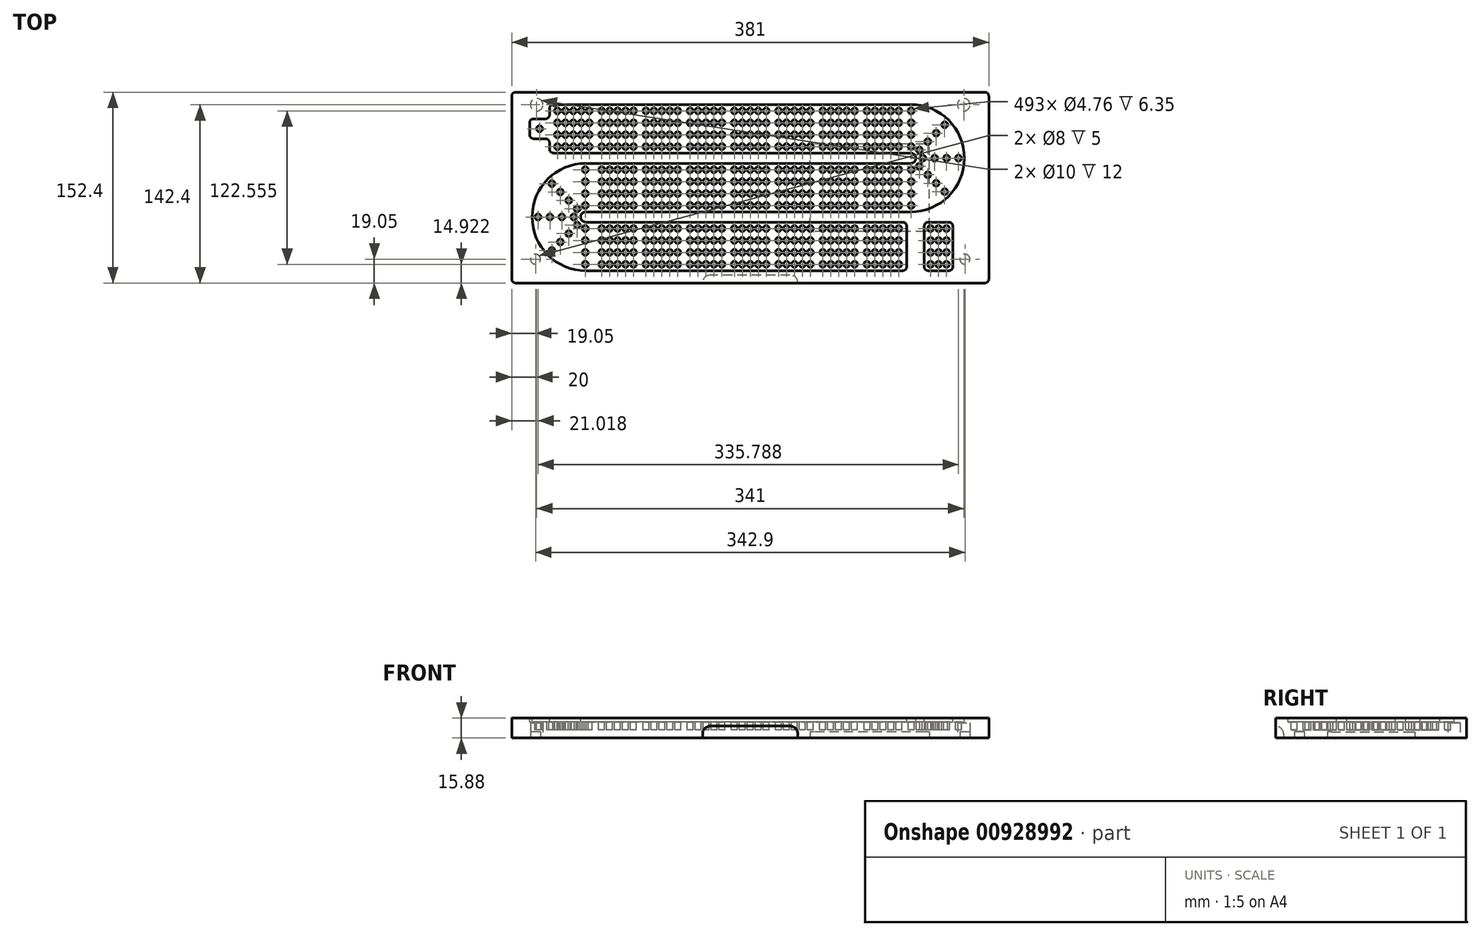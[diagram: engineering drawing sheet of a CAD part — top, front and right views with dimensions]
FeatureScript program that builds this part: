
annotation { "Feature Type Name" : "Feature", "Feature Type Description" : "" }
export const myFeature = defineFeature(function(context is Context, id is Id, definition is map)
    precondition{}
    {
        {
            var Q0;
            Q0=qCreatedBy(makeId("Top.planeOp"),FACE);
            var sketch = newSketch(context, id + "F0", { "sketchPlane" : qUnion([Q0])});
            skLineSegment(sketch, "E0.bottom", {"start": v(190.5, -76.2) * mm, "end": v(-190.5, -76.2) * mm});
            skLineSegment(sketch, "E0.top", {"start": v(190.5, 76.2) * mm, "end": v(-190.5, 76.2) * mm});
            skLineSegment(sketch, "E0.left", {"start": v(190.5, -76.2) * mm, "end": v(190.5, 76.2) * mm});
            skLineSegment(sketch, "E0.right", {"start": v(-190.5, -76.2) * mm, "end": v(-190.5, 76.2) * mm});
            skPoint(sketch, "E0.middle", {"position": v(0, 0) * mm});
            skSolve(sketch);
        }
        {
            var Q0;
            Q0=makeQuery(id+"F0.imprint","IMPRINT",FACE,{"disambiguationData":[TD([[makeQuery(id+"F0.imprint","IMPRINT",EDGE,{"derivedFrom":sQuery(id+"F0.wireOp",EDGE,"E0.bottom")}),-1.0]])]});
            extrude(context, id + "F1", {"entities" : qUnion([Q0]), "oppositeDirection" : true, "depth" : 15.88 * mm, "offsetDistance" : 25.4 * mm});
        }
        {
            var Q0;
            Q0=makeQuery(id+"F1.opExtrude","CAP_FACE",FACE,{"disambiguationData":[OSD([sQuery(id+"F0.wireOp",EDGE,"E0.bottom"),sQuery(id+"F0.wireOp",EDGE,"E0.top"),sQuery(id+"F0.wireOp",EDGE,"E0.left"),sQuery(id+"F0.wireOp",EDGE,"E0.right")])],"isStart":true});
            var sketch = newSketch(context, id + "F2", { "sketchPlane" : qUnion([Q0])});
            skCircle(sketch, "E1", {"center": v(0, -14.29) * mm, "radius": 2.38 * mm});
            skCircle(sketch, "E2.0.1.0", {"center": v(0, -4.76) * mm, "radius": 2.38 * mm});
            skCircle(sketch, "E2.0.2.0", {"center": v(0, 4.76) * mm, "radius": 2.38 * mm});
            skCircle(sketch, "E2.0.3.0", {"center": v(0, 14.29) * mm, "radius": 2.38 * mm});
            skCircle(sketch, "E2.1.0.0", {"center": v(6.35, -14.29) * mm, "radius": 2.38 * mm});
            skCircle(sketch, "E2.1.1.0", {"center": v(6.35, -4.76) * mm, "radius": 2.38 * mm});
            skCircle(sketch, "E2.1.2.0", {"center": v(6.35, 4.76) * mm, "radius": 2.38 * mm});
            skCircle(sketch, "E2.1.3.0", {"center": v(6.35, 14.29) * mm, "radius": 2.38 * mm});
            skCircle(sketch, "E2.2.0.0", {"center": v(12.7, -14.29) * mm, "radius": 2.38 * mm});
            skCircle(sketch, "E2.2.1.0", {"center": v(12.7, -4.76) * mm, "radius": 2.38 * mm});
            skCircle(sketch, "E2.2.2.0", {"center": v(12.7, 4.76) * mm, "radius": 2.38 * mm});
            skCircle(sketch, "E2.2.3.0", {"center": v(12.7, 14.29) * mm, "radius": 2.38 * mm});
            skCircle(sketch, "E3.1.0.0", {"center": v(-6.35, -14.29) * mm, "radius": 2.38 * mm});
            skCircle(sketch, "E3.2.0.0", {"center": v(-12.7, -14.29) * mm, "radius": 2.38 * mm});
            skCircle(sketch, "E4.0.1.0", {"center": v(-6.35, -4.76) * mm, "radius": 2.38 * mm});
            skCircle(sketch, "E4.0.2.0", {"center": v(-6.35, 4.76) * mm, "radius": 2.38 * mm});
            skCircle(sketch, "E4.0.3.0", {"center": v(-6.35, 14.29) * mm, "radius": 2.38 * mm});
            skCircle(sketch, "E5.0.1.0", {"center": v(-12.7, -4.76) * mm, "radius": 2.38 * mm});
            skCircle(sketch, "E5.0.2.0", {"center": v(-12.7, 4.76) * mm, "radius": 2.38 * mm});
            skCircle(sketch, "E5.0.3.0", {"center": v(-12.7, 14.29) * mm, "radius": 2.38 * mm});
            skCircle(sketch, "E6.1.0.0", {"center": v(28.96, 4.76) * mm, "radius": 2.38 * mm});
            skCircle(sketch, "E6.1.0.1", {"center": v(41.66, -14.29) * mm, "radius": 2.38 * mm});
            skCircle(sketch, "E6.1.0.2", {"center": v(41.66, -4.76) * mm, "radius": 2.38 * mm});
            skCircle(sketch, "E6.1.0.3", {"center": v(41.66, 14.29) * mm, "radius": 2.38 * mm});
            skCircle(sketch, "E6.1.0.4", {"center": v(48, 14.29) * mm, "radius": 2.38 * mm});
            skCircle(sketch, "E6.1.0.5", {"center": v(22.6, -14.29) * mm, "radius": 2.38 * mm});
            skCircle(sketch, "E6.1.0.6", {"center": v(28.96, -4.76) * mm, "radius": 2.38 * mm});
            skCircle(sketch, "E6.1.0.7", {"center": v(48, -4.76) * mm, "radius": 2.38 * mm});
            skCircle(sketch, "E6.1.0.8", {"center": v(35.3, 14.29) * mm, "radius": 2.38 * mm});
            skCircle(sketch, "E6.1.0.9", {"center": v(28.96, -14.29) * mm, "radius": 2.38 * mm});
            skCircle(sketch, "E6.1.0.10", {"center": v(22.6, -4.76) * mm, "radius": 2.38 * mm});
            skCircle(sketch, "E6.1.0.11", {"center": v(48, -14.29) * mm, "radius": 2.38 * mm});
            skCircle(sketch, "E6.1.0.12", {"center": v(35.3, -14.29) * mm, "radius": 2.38 * mm});
            skCircle(sketch, "E6.1.0.13", {"center": v(35.3, -4.76) * mm, "radius": 2.38 * mm});
            skCircle(sketch, "E6.1.0.14", {"center": v(28.96, 14.29) * mm, "radius": 2.38 * mm});
            skCircle(sketch, "E6.1.0.15", {"center": v(41.66, 4.76) * mm, "radius": 2.38 * mm});
            skCircle(sketch, "E6.1.0.16", {"center": v(22.6, 14.29) * mm, "radius": 2.38 * mm});
            skCircle(sketch, "E6.1.0.17", {"center": v(48, 4.76) * mm, "radius": 2.38 * mm});
            skCircle(sketch, "E6.1.0.18", {"center": v(22.6, 4.76) * mm, "radius": 2.38 * mm});
            skCircle(sketch, "E6.1.0.19", {"center": v(35.3, 4.76) * mm, "radius": 2.38 * mm});
            skCircle(sketch, "E6.2.0.0", {"center": v(64.26, 4.76) * mm, "radius": 2.38 * mm});
            skCircle(sketch, "E6.2.0.1", {"center": v(76.96, -14.29) * mm, "radius": 2.38 * mm});
            skCircle(sketch, "E6.2.0.2", {"center": v(76.96, -4.76) * mm, "radius": 2.38 * mm});
            skCircle(sketch, "E6.2.0.3", {"center": v(76.96, 14.29) * mm, "radius": 2.38 * mm});
            skCircle(sketch, "E6.2.0.4", {"center": v(83.31, 14.29) * mm, "radius": 2.38 * mm});
            skCircle(sketch, "E6.2.0.5", {"center": v(57.91, -14.29) * mm, "radius": 2.38 * mm});
            skCircle(sketch, "E6.2.0.6", {"center": v(64.26, -4.76) * mm, "radius": 2.38 * mm});
            skCircle(sketch, "E6.2.0.7", {"center": v(83.31, -4.76) * mm, "radius": 2.38 * mm});
            skCircle(sketch, "E6.2.0.8", {"center": v(70.61, 14.29) * mm, "radius": 2.38 * mm});
            skCircle(sketch, "E6.2.0.9", {"center": v(64.26, -14.29) * mm, "radius": 2.38 * mm});
            skCircle(sketch, "E6.2.0.10", {"center": v(57.91, -4.76) * mm, "radius": 2.38 * mm});
            skCircle(sketch, "E6.2.0.11", {"center": v(83.31, -14.29) * mm, "radius": 2.38 * mm});
            skCircle(sketch, "E6.2.0.12", {"center": v(70.61, -14.29) * mm, "radius": 2.38 * mm});
            skCircle(sketch, "E6.2.0.13", {"center": v(70.61, -4.76) * mm, "radius": 2.38 * mm});
            skCircle(sketch, "E6.2.0.14", {"center": v(64.26, 14.29) * mm, "radius": 2.38 * mm});
            skCircle(sketch, "E6.2.0.15", {"center": v(76.96, 4.76) * mm, "radius": 2.38 * mm});
            skCircle(sketch, "E6.2.0.16", {"center": v(57.91, 14.29) * mm, "radius": 2.38 * mm});
            skCircle(sketch, "E6.2.0.17", {"center": v(83.31, 4.76) * mm, "radius": 2.38 * mm});
            skCircle(sketch, "E6.2.0.18", {"center": v(57.91, 4.76) * mm, "radius": 2.38 * mm});
            skCircle(sketch, "E6.2.0.19", {"center": v(70.61, 4.76) * mm, "radius": 2.38 * mm});
            skCircle(sketch, "E6.3.0.0", {"center": v(99.57, 4.76) * mm, "radius": 2.38 * mm});
            skCircle(sketch, "E6.3.0.1", {"center": v(112.27, -14.29) * mm, "radius": 2.38 * mm});
            skCircle(sketch, "E6.3.0.2", {"center": v(112.27, -4.76) * mm, "radius": 2.38 * mm});
            skCircle(sketch, "E6.3.0.3", {"center": v(112.27, 14.29) * mm, "radius": 2.38 * mm});
            skCircle(sketch, "E6.3.0.4", {"center": v(118.62, 14.29) * mm, "radius": 2.38 * mm});
            skCircle(sketch, "E6.3.0.5", {"center": v(93.22, -14.29) * mm, "radius": 2.38 * mm});
            skCircle(sketch, "E6.3.0.6", {"center": v(99.57, -4.76) * mm, "radius": 2.38 * mm});
            skCircle(sketch, "E6.3.0.7", {"center": v(118.62, -4.76) * mm, "radius": 2.38 * mm});
            skCircle(sketch, "E6.3.0.8", {"center": v(105.92, 14.29) * mm, "radius": 2.38 * mm});
            skCircle(sketch, "E6.3.0.9", {"center": v(99.57, -14.29) * mm, "radius": 2.38 * mm});
            skCircle(sketch, "E6.3.0.10", {"center": v(93.22, -4.76) * mm, "radius": 2.38 * mm});
            skCircle(sketch, "E6.3.0.11", {"center": v(118.62, -14.29) * mm, "radius": 2.38 * mm});
            skCircle(sketch, "E6.3.0.12", {"center": v(105.92, -14.29) * mm, "radius": 2.38 * mm});
            skCircle(sketch, "E6.3.0.13", {"center": v(105.92, -4.76) * mm, "radius": 2.38 * mm});
            skCircle(sketch, "E6.3.0.14", {"center": v(99.57, 14.29) * mm, "radius": 2.38 * mm});
            skCircle(sketch, "E6.3.0.15", {"center": v(112.27, 4.76) * mm, "radius": 2.38 * mm});
            skCircle(sketch, "E6.3.0.16", {"center": v(93.22, 14.29) * mm, "radius": 2.38 * mm});
            skCircle(sketch, "E6.3.0.17", {"center": v(118.62, 4.76) * mm, "radius": 2.38 * mm});
            skCircle(sketch, "E6.3.0.18", {"center": v(93.22, 4.76) * mm, "radius": 2.38 * mm});
            skCircle(sketch, "E6.3.0.19", {"center": v(105.92, 4.76) * mm, "radius": 2.38 * mm});
            skLineSegment(sketch, "E6.direction1", {"start": v(-12.7, -14.29) * mm, "end": v(22.6, -14.29) * mm, "construction": true});
            skCircle(sketch, "E7.1.0.0", {"center": v(-48, 4.76) * mm, "radius": 2.38 * mm});
            skCircle(sketch, "E7.1.0.1", {"center": v(-48, -14.29) * mm, "radius": 2.38 * mm});
            skCircle(sketch, "E7.1.0.2", {"center": v(-22.6, 14.29) * mm, "radius": 2.38 * mm});
            skCircle(sketch, "E7.1.0.3", {"center": v(-35.3, 4.76) * mm, "radius": 2.38 * mm});
            skCircle(sketch, "E7.1.0.4", {"center": v(-48, 14.29) * mm, "radius": 2.38 * mm});
            skCircle(sketch, "E7.1.0.5", {"center": v(-35.3, -14.29) * mm, "radius": 2.38 * mm});
            skCircle(sketch, "E7.1.0.6", {"center": v(-35.3, -4.76) * mm, "radius": 2.38 * mm});
            skCircle(sketch, "E7.1.0.7", {"center": v(-48, -4.76) * mm, "radius": 2.38 * mm});
            skCircle(sketch, "E7.1.0.8", {"center": v(-28.96, -4.76) * mm, "radius": 2.38 * mm});
            skCircle(sketch, "E7.1.0.9", {"center": v(-41.66, -4.76) * mm, "radius": 2.38 * mm});
            skCircle(sketch, "E7.1.0.10", {"center": v(-28.96, 4.76) * mm, "radius": 2.38 * mm});
            skCircle(sketch, "E7.1.0.11", {"center": v(-22.6, -4.76) * mm, "radius": 2.38 * mm});
            skCircle(sketch, "E7.1.0.12", {"center": v(-41.66, 14.29) * mm, "radius": 2.38 * mm});
            skCircle(sketch, "E7.1.0.13", {"center": v(-22.6, 4.76) * mm, "radius": 2.38 * mm});
            skCircle(sketch, "E7.1.0.14", {"center": v(-41.66, 4.76) * mm, "radius": 2.38 * mm});
            skCircle(sketch, "E7.1.0.15", {"center": v(-35.3, 14.29) * mm, "radius": 2.38 * mm});
            skCircle(sketch, "E7.1.0.16", {"center": v(-28.96, -14.29) * mm, "radius": 2.38 * mm});
            skCircle(sketch, "E7.1.0.17", {"center": v(-28.96, 14.29) * mm, "radius": 2.38 * mm});
            skCircle(sketch, "E7.1.0.18", {"center": v(-41.66, -14.29) * mm, "radius": 2.38 * mm});
            skCircle(sketch, "E7.1.0.19", {"center": v(-22.6, -14.29) * mm, "radius": 2.38 * mm});
            skCircle(sketch, "E7.2.0.0", {"center": v(-83.31, 4.76) * mm, "radius": 2.38 * mm});
            skCircle(sketch, "E7.2.0.1", {"center": v(-83.31, -14.29) * mm, "radius": 2.38 * mm});
            skCircle(sketch, "E7.2.0.2", {"center": v(-57.91, 14.29) * mm, "radius": 2.38 * mm});
            skCircle(sketch, "E7.2.0.3", {"center": v(-70.61, 4.76) * mm, "radius": 2.38 * mm});
            skCircle(sketch, "E7.2.0.4", {"center": v(-83.31, 14.29) * mm, "radius": 2.38 * mm});
            skCircle(sketch, "E7.2.0.5", {"center": v(-70.61, -14.29) * mm, "radius": 2.38 * mm});
            skCircle(sketch, "E7.2.0.6", {"center": v(-70.61, -4.76) * mm, "radius": 2.38 * mm});
            skCircle(sketch, "E7.2.0.7", {"center": v(-83.31, -4.76) * mm, "radius": 2.38 * mm});
            skCircle(sketch, "E7.2.0.8", {"center": v(-64.26, -4.76) * mm, "radius": 2.38 * mm});
            skCircle(sketch, "E7.2.0.9", {"center": v(-76.96, -4.76) * mm, "radius": 2.38 * mm});
            skCircle(sketch, "E7.2.0.10", {"center": v(-64.26, 4.76) * mm, "radius": 2.38 * mm});
            skCircle(sketch, "E7.2.0.11", {"center": v(-57.91, -4.76) * mm, "radius": 2.38 * mm});
            skCircle(sketch, "E7.2.0.12", {"center": v(-76.96, 14.29) * mm, "radius": 2.38 * mm});
            skCircle(sketch, "E7.2.0.13", {"center": v(-57.91, 4.76) * mm, "radius": 2.38 * mm});
            skCircle(sketch, "E7.2.0.14", {"center": v(-76.96, 4.76) * mm, "radius": 2.38 * mm});
            skCircle(sketch, "E7.2.0.15", {"center": v(-70.61, 14.29) * mm, "radius": 2.38 * mm});
            skCircle(sketch, "E7.2.0.16", {"center": v(-64.26, -14.29) * mm, "radius": 2.38 * mm});
            skCircle(sketch, "E7.2.0.17", {"center": v(-64.26, 14.29) * mm, "radius": 2.38 * mm});
            skCircle(sketch, "E7.2.0.18", {"center": v(-76.96, -14.29) * mm, "radius": 2.38 * mm});
            skCircle(sketch, "E7.2.0.19", {"center": v(-57.91, -14.29) * mm, "radius": 2.38 * mm});
            skCircle(sketch, "E7.3.0.0", {"center": v(-118.62, 4.76) * mm, "radius": 2.38 * mm});
            skCircle(sketch, "E7.3.0.1", {"center": v(-118.62, -14.29) * mm, "radius": 2.38 * mm});
            skCircle(sketch, "E7.3.0.2", {"center": v(-93.22, 14.29) * mm, "radius": 2.38 * mm});
            skCircle(sketch, "E7.3.0.3", {"center": v(-105.92, 4.76) * mm, "radius": 2.38 * mm});
            skCircle(sketch, "E7.3.0.4", {"center": v(-118.62, 14.29) * mm, "radius": 2.38 * mm});
            skCircle(sketch, "E7.3.0.5", {"center": v(-105.92, -14.29) * mm, "radius": 2.38 * mm});
            skCircle(sketch, "E7.3.0.6", {"center": v(-105.92, -4.76) * mm, "radius": 2.38 * mm});
            skCircle(sketch, "E7.3.0.7", {"center": v(-118.62, -4.76) * mm, "radius": 2.38 * mm});
            skCircle(sketch, "E7.3.0.8", {"center": v(-99.57, -4.76) * mm, "radius": 2.38 * mm});
            skCircle(sketch, "E7.3.0.9", {"center": v(-112.27, -4.76) * mm, "radius": 2.38 * mm});
            skCircle(sketch, "E7.3.0.10", {"center": v(-99.57, 4.76) * mm, "radius": 2.38 * mm});
            skCircle(sketch, "E7.3.0.11", {"center": v(-93.22, -4.76) * mm, "radius": 2.38 * mm});
            skCircle(sketch, "E7.3.0.12", {"center": v(-112.27, 14.29) * mm, "radius": 2.38 * mm});
            skCircle(sketch, "E7.3.0.13", {"center": v(-93.22, 4.76) * mm, "radius": 2.38 * mm});
            skCircle(sketch, "E7.3.0.14", {"center": v(-112.27, 4.76) * mm, "radius": 2.38 * mm});
            skCircle(sketch, "E7.3.0.15", {"center": v(-105.92, 14.29) * mm, "radius": 2.38 * mm});
            skCircle(sketch, "E7.3.0.16", {"center": v(-99.57, -14.29) * mm, "radius": 2.38 * mm});
            skCircle(sketch, "E7.3.0.17", {"center": v(-99.57, 14.29) * mm, "radius": 2.38 * mm});
            skCircle(sketch, "E7.3.0.18", {"center": v(-112.27, -14.29) * mm, "radius": 2.38 * mm});
            skCircle(sketch, "E7.3.0.19", {"center": v(-93.22, -14.29) * mm, "radius": 2.38 * mm});
            skCircle(sketch, "E8.0.1.0", {"center": v(93.22, 61.28) * mm, "radius": 2.38 * mm});
            skCircle(sketch, "E8.0.1.1", {"center": v(-83.31, 32.7) * mm, "radius": 2.38 * mm});
            skCircle(sketch, "E8.0.1.2", {"center": v(0, 61.28) * mm, "radius": 2.38 * mm});
            skCircle(sketch, "E8.0.1.3", {"center": v(48, 51.75) * mm, "radius": 2.38 * mm});
            skCircle(sketch, "E8.0.1.4", {"center": v(-41.66, 32.7) * mm, "radius": 2.38 * mm});
            skCircle(sketch, "E8.0.1.5", {"center": v(-105.92, 42.23) * mm, "radius": 2.38 * mm});
            skCircle(sketch, "E8.0.1.6", {"center": v(35.3, 32.7) * mm, "radius": 2.38 * mm});
            skCircle(sketch, "E8.0.1.7", {"center": v(48, 42.23) * mm, "radius": 2.38 * mm});
            skCircle(sketch, "E8.0.1.8", {"center": v(22.6, 42.23) * mm, "radius": 2.38 * mm});
            skCircle(sketch, "E8.0.1.9", {"center": v(-112.27, 61.28) * mm, "radius": 2.38 * mm});
            skCircle(sketch, "E8.0.1.10", {"center": v(0, 42.23) * mm, "radius": 2.38 * mm});
            skCircle(sketch, "E8.0.1.11", {"center": v(76.96, 42.23) * mm, "radius": 2.38 * mm});
            skCircle(sketch, "E8.0.1.12", {"center": v(-70.61, 42.23) * mm, "radius": 2.38 * mm});
            skCircle(sketch, "E8.0.1.13", {"center": v(64.26, 61.28) * mm, "radius": 2.38 * mm});
            skCircle(sketch, "E8.0.1.14", {"center": v(-35.3, 42.23) * mm, "radius": 2.38 * mm});
            skCircle(sketch, "E8.0.1.15", {"center": v(-83.31, 42.23) * mm, "radius": 2.38 * mm});
            skCircle(sketch, "E8.0.1.16", {"center": v(76.96, 32.7) * mm, "radius": 2.38 * mm});
            skCircle(sketch, "E8.0.1.17", {"center": v(-118.62, 32.7) * mm, "radius": 2.38 * mm});
            skCircle(sketch, "E8.0.1.18", {"center": v(35.3, 42.23) * mm, "radius": 2.38 * mm});
            skCircle(sketch, "E8.0.1.19", {"center": v(-99.57, 51.75) * mm, "radius": 2.38 * mm});
            skCircle(sketch, "E8.0.1.20", {"center": v(105.92, 61.28) * mm, "radius": 2.38 * mm});
            skCircle(sketch, "E8.0.1.21", {"center": v(99.57, 61.28) * mm, "radius": 2.38 * mm});
            skCircle(sketch, "E8.0.1.22", {"center": v(70.61, 42.23) * mm, "radius": 2.38 * mm});
            skCircle(sketch, "E8.0.1.23", {"center": v(28.96, 51.75) * mm, "radius": 2.38 * mm});
            skCircle(sketch, "E8.0.1.24", {"center": v(93.22, 51.75) * mm, "radius": 2.38 * mm});
            skCircle(sketch, "E8.0.1.25", {"center": v(48, 32.7) * mm, "radius": 2.38 * mm});
            skCircle(sketch, "E8.0.1.26", {"center": v(-28.96, 61.28) * mm, "radius": 2.38 * mm});
            skCircle(sketch, "E8.0.1.27", {"center": v(-70.61, 61.28) * mm, "radius": 2.38 * mm});
            skCircle(sketch, "E8.0.1.28", {"center": v(-112.27, 42.23) * mm, "radius": 2.38 * mm});
            skCircle(sketch, "E8.0.1.29", {"center": v(-99.57, 32.7) * mm, "radius": 2.38 * mm});
            skCircle(sketch, "E8.0.1.30", {"center": v(6.35, 61.28) * mm, "radius": 2.38 * mm});
            skCircle(sketch, "E8.0.1.31", {"center": v(12.7, 61.28) * mm, "radius": 2.38 * mm});
            skCircle(sketch, "E8.0.1.32", {"center": v(-22.6, 51.75) * mm, "radius": 2.38 * mm});
            skCircle(sketch, "E8.0.1.33", {"center": v(99.57, 42.23) * mm, "radius": 2.38 * mm});
            skCircle(sketch, "E8.0.1.35", {"center": v(64.26, 51.75) * mm, "radius": 2.38 * mm});
            skCircle(sketch, "E8.0.1.36", {"center": v(6.35, 42.23) * mm, "radius": 2.38 * mm});
            skCircle(sketch, "E8.0.1.37", {"center": v(57.91, 61.28) * mm, "radius": 2.38 * mm});
            skCircle(sketch, "E8.0.1.38", {"center": v(-64.26, 32.7) * mm, "radius": 2.38 * mm});
            skCircle(sketch, "E8.0.1.39", {"center": v(-118.62, 42.23) * mm, "radius": 2.38 * mm});
            skCircle(sketch, "E8.0.1.40", {"center": v(-12.7, 61.28) * mm, "radius": 2.38 * mm});
            skCircle(sketch, "E8.0.1.41", {"center": v(-83.31, 51.75) * mm, "radius": 2.38 * mm});
            skCircle(sketch, "E8.0.1.42", {"center": v(112.27, 61.28) * mm, "radius": 2.38 * mm});
            skCircle(sketch, "E8.0.1.43", {"center": v(-70.61, 32.7) * mm, "radius": 2.38 * mm});
            skCircle(sketch, "E8.0.1.44", {"center": v(-28.96, 51.75) * mm, "radius": 2.38 * mm});
            skCircle(sketch, "E8.0.1.45", {"center": v(28.96, 61.28) * mm, "radius": 2.38 * mm});
            skCircle(sketch, "E8.0.1.46", {"center": v(12.7, 42.23) * mm, "radius": 2.38 * mm});
            skCircle(sketch, "E8.0.1.47", {"center": v(-12.7, 51.75) * mm, "radius": 2.38 * mm});
            skCircle(sketch, "E8.0.1.48", {"center": v(-41.66, 42.23) * mm, "radius": 2.38 * mm});
            skCircle(sketch, "E8.0.1.49", {"center": v(64.26, 32.7) * mm, "radius": 2.38 * mm});
            skCircle(sketch, "E8.0.1.50", {"center": v(22.6, 61.28) * mm, "radius": 2.38 * mm});
            skCircle(sketch, "E8.0.1.51", {"center": v(76.96, 61.28) * mm, "radius": 2.38 * mm});
            skCircle(sketch, "E8.0.1.52", {"center": v(-99.57, 42.23) * mm, "radius": 2.38 * mm});
            skCircle(sketch, "E8.0.1.53", {"center": v(93.22, 32.7) * mm, "radius": 2.38 * mm});
            skCircle(sketch, "E8.0.1.54", {"center": v(118.62, 61.28) * mm, "radius": 2.38 * mm});
            skCircle(sketch, "E8.0.1.55", {"center": v(-12.7, 42.23) * mm, "radius": 2.38 * mm});
            skCircle(sketch, "E8.0.1.56", {"center": v(-41.66, 61.28) * mm, "radius": 2.38 * mm});
            skCircle(sketch, "E8.0.1.57", {"center": v(-93.22, 51.75) * mm, "radius": 2.38 * mm});
            skCircle(sketch, "E8.0.1.58", {"center": v(6.35, 51.75) * mm, "radius": 2.38 * mm});
            skCircle(sketch, "E8.0.1.59", {"center": v(118.62, 42.23) * mm, "radius": 2.38 * mm});
            skCircle(sketch, "E8.0.1.60", {"center": v(93.22, 42.23) * mm, "radius": 2.38 * mm});
            skCircle(sketch, "E8.0.1.61", {"center": v(112.27, 42.23) * mm, "radius": 2.38 * mm});
            skCircle(sketch, "E8.0.1.62", {"center": v(-57.91, 51.75) * mm, "radius": 2.38 * mm});
            skCircle(sketch, "E8.0.1.63", {"center": v(-76.96, 61.28) * mm, "radius": 2.38 * mm});
            skCircle(sketch, "E8.0.1.64", {"center": v(-12.7, 32.7) * mm, "radius": 2.38 * mm});
            skCircle(sketch, "E8.0.1.65", {"center": v(83.31, 61.28) * mm, "radius": 2.38 * mm});
            skCircle(sketch, "E8.0.1.66", {"center": v(-93.22, 61.28) * mm, "radius": 2.38 * mm});
            skCircle(sketch, "E8.0.1.67", {"center": v(-57.91, 32.7) * mm, "radius": 2.38 * mm});
            skCircle(sketch, "E8.0.1.68", {"center": v(-99.57, 61.28) * mm, "radius": 2.38 * mm});
            skCircle(sketch, "E8.0.1.69", {"center": v(41.66, 61.28) * mm, "radius": 2.38 * mm});
            skCircle(sketch, "E8.0.1.70", {"center": v(-83.31, 61.28) * mm, "radius": 2.38 * mm});
            skCircle(sketch, "E8.0.1.71", {"center": v(57.91, 42.23) * mm, "radius": 2.38 * mm});
            skCircle(sketch, "E8.0.1.72", {"center": v(-28.96, 42.23) * mm, "radius": 2.38 * mm});
            skCircle(sketch, "E8.0.1.73", {"center": v(105.92, 32.7) * mm, "radius": 2.38 * mm});
            skCircle(sketch, "E8.0.1.74", {"center": v(-6.35, 42.23) * mm, "radius": 2.38 * mm});
            skCircle(sketch, "E8.0.1.75", {"center": v(-35.3, 61.28) * mm, "radius": 2.38 * mm});
            skCircle(sketch, "E8.0.1.76", {"center": v(-105.92, 61.28) * mm, "radius": 2.38 * mm});
            skCircle(sketch, "E8.0.1.77", {"center": v(83.31, 51.75) * mm, "radius": 2.38 * mm});
            skCircle(sketch, "E8.0.1.78", {"center": v(41.66, 42.23) * mm, "radius": 2.38 * mm});
            skCircle(sketch, "E8.0.1.79", {"center": v(-93.22, 42.23) * mm, "radius": 2.38 * mm});
            skCircle(sketch, "E8.0.1.80", {"center": v(28.96, 42.23) * mm, "radius": 2.38 * mm});
            skCircle(sketch, "E8.0.1.81", {"center": v(48, 61.28) * mm, "radius": 2.38 * mm});
            skCircle(sketch, "E8.0.1.82", {"center": v(35.3, 61.28) * mm, "radius": 2.38 * mm});
            skCircle(sketch, "E8.0.1.83", {"center": v(-76.96, 42.23) * mm, "radius": 2.38 * mm});
            skCircle(sketch, "E8.0.1.84", {"center": v(-93.22, 32.7) * mm, "radius": 2.38 * mm});
            skCircle(sketch, "E8.0.1.85", {"center": v(64.26, 42.23) * mm, "radius": 2.38 * mm});
            skCircle(sketch, "E8.0.1.86", {"center": v(-57.91, 42.23) * mm, "radius": 2.38 * mm});
            skCircle(sketch, "E8.0.1.87", {"center": v(-48, 61.28) * mm, "radius": 2.38 * mm});
            skCircle(sketch, "E8.0.1.88", {"center": v(-41.66, 51.75) * mm, "radius": 2.38 * mm});
            skCircle(sketch, "E8.0.1.89", {"center": v(-28.96, 32.7) * mm, "radius": 2.38 * mm});
            skCircle(sketch, "E8.0.1.90", {"center": v(83.31, 42.23) * mm, "radius": 2.38 * mm});
            skCircle(sketch, "E8.0.1.91", {"center": v(-22.6, 42.23) * mm, "radius": 2.38 * mm});
            skCircle(sketch, "E8.0.1.92", {"center": v(-64.26, 61.28) * mm, "radius": 2.38 * mm});
            skCircle(sketch, "E8.0.1.93", {"center": v(-57.91, 61.28) * mm, "radius": 2.38 * mm});
            skCircle(sketch, "E8.0.1.94", {"center": v(70.61, 61.28) * mm, "radius": 2.38 * mm});
            skCircle(sketch, "E8.0.1.95", {"center": v(-118.62, 51.75) * mm, "radius": 2.38 * mm});
            skCircle(sketch, "E8.0.1.96", {"center": v(112.27, 51.75) * mm, "radius": 2.38 * mm});
            skCircle(sketch, "E8.0.1.97", {"center": v(-64.26, 51.75) * mm, "radius": 2.38 * mm});
            skCircle(sketch, "E8.0.1.98", {"center": v(-6.35, 61.28) * mm, "radius": 2.38 * mm});
            skCircle(sketch, "E8.0.1.99", {"center": v(-64.26, 42.23) * mm, "radius": 2.38 * mm});
            skCircle(sketch, "E8.0.1.100", {"center": v(-70.61, 51.75) * mm, "radius": 2.38 * mm});
            skCircle(sketch, "E8.0.1.101", {"center": v(-22.6, 61.28) * mm, "radius": 2.38 * mm});
            skCircle(sketch, "E8.0.1.102", {"center": v(105.92, 42.23) * mm, "radius": 2.38 * mm});
            skCircle(sketch, "E8.0.1.103", {"center": v(-48, 42.23) * mm, "radius": 2.38 * mm});
            skCircle(sketch, "E8.0.1.104", {"center": v(-118.62, 61.28) * mm, "radius": 2.38 * mm});
            skCircle(sketch, "E8.0.1.105", {"center": v(57.91, 32.7) * mm, "radius": 2.38 * mm});
            skCircle(sketch, "E8.0.1.106", {"center": v(0, 32.7) * mm, "radius": 2.38 * mm});
            skCircle(sketch, "E8.0.1.107", {"center": v(0, 51.75) * mm, "radius": 2.38 * mm});
            skCircle(sketch, "E8.0.1.108", {"center": v(-112.27, 51.75) * mm, "radius": 2.38 * mm});
            skCircle(sketch, "E8.0.1.109", {"center": v(-76.96, 51.75) * mm, "radius": 2.38 * mm});
            skCircle(sketch, "E8.0.1.110", {"center": v(-6.35, 51.75) * mm, "radius": 2.38 * mm});
            skCircle(sketch, "E8.0.1.111", {"center": v(118.62, 32.7) * mm, "radius": 2.38 * mm});
            skCircle(sketch, "E8.0.1.112", {"center": v(-112.27, 32.7) * mm, "radius": 2.38 * mm});
            skCircle(sketch, "E8.0.1.113", {"center": v(83.31, 32.7) * mm, "radius": 2.38 * mm});
            skCircle(sketch, "E8.0.1.114", {"center": v(-48, 51.75) * mm, "radius": 2.38 * mm});
            skCircle(sketch, "E8.0.1.115", {"center": v(-6.35, 32.7) * mm, "radius": 2.38 * mm});
            skCircle(sketch, "E8.0.1.116", {"center": v(99.57, 32.7) * mm, "radius": 2.38 * mm});
            skCircle(sketch, "E8.0.1.117", {"center": v(-22.6, 32.7) * mm, "radius": 2.38 * mm});
            skCircle(sketch, "E8.0.1.118", {"center": v(-105.92, 51.75) * mm, "radius": 2.38 * mm});
            skCircle(sketch, "E8.0.1.119", {"center": v(6.35, 32.7) * mm, "radius": 2.38 * mm});
            skCircle(sketch, "E8.0.1.120", {"center": v(28.96, 32.7) * mm, "radius": 2.38 * mm});
            skCircle(sketch, "E8.0.1.121", {"center": v(57.91, 51.75) * mm, "radius": 2.38 * mm});
            skCircle(sketch, "E8.0.1.122", {"center": v(112.27, 32.7) * mm, "radius": 2.38 * mm});
            skCircle(sketch, "E8.0.1.123", {"center": v(118.62, 51.75) * mm, "radius": 2.38 * mm});
            skCircle(sketch, "E8.0.1.124", {"center": v(-105.92, 32.7) * mm, "radius": 2.38 * mm});
            skCircle(sketch, "E8.0.1.125", {"center": v(70.61, 32.7) * mm, "radius": 2.38 * mm});
            skCircle(sketch, "E8.0.1.126", {"center": v(12.7, 32.7) * mm, "radius": 2.38 * mm});
            skCircle(sketch, "E8.0.1.127", {"center": v(22.6, 51.75) * mm, "radius": 2.38 * mm});
            skCircle(sketch, "E8.0.1.128", {"center": v(-35.3, 32.7) * mm, "radius": 2.38 * mm});
            skCircle(sketch, "E8.0.1.129", {"center": v(105.92, 51.75) * mm, "radius": 2.38 * mm});
            skCircle(sketch, "E8.0.1.130", {"center": v(-76.96, 32.7) * mm, "radius": 2.38 * mm});
            skCircle(sketch, "E8.0.1.131", {"center": v(-35.3, 51.75) * mm, "radius": 2.38 * mm});
            skCircle(sketch, "E8.0.1.132", {"center": v(41.66, 51.75) * mm, "radius": 2.38 * mm});
            skCircle(sketch, "E8.0.1.133", {"center": v(99.57, 51.75) * mm, "radius": 2.38 * mm});
            skCircle(sketch, "E8.0.1.134", {"center": v(70.61, 51.75) * mm, "radius": 2.38 * mm});
            skCircle(sketch, "E8.0.1.135", {"center": v(-48, 32.7) * mm, "radius": 2.38 * mm});
            skCircle(sketch, "E8.0.1.136", {"center": v(12.7, 51.75) * mm, "radius": 2.38 * mm});
            skCircle(sketch, "E8.0.1.137", {"center": v(35.3, 51.75) * mm, "radius": 2.38 * mm});
            skCircle(sketch, "E8.0.1.138", {"center": v(41.66, 32.7) * mm, "radius": 2.38 * mm});
            skCircle(sketch, "E8.0.1.139", {"center": v(76.96, 51.75) * mm, "radius": 2.38 * mm});
            skCircle(sketch, "E8.0.1.140", {"center": v(22.6, 32.7) * mm, "radius": 2.38 * mm});
            skCircle(sketch, "E9.0.1.0", {"center": v(-76.96, -61.28) * mm, "radius": 2.38 * mm});
            skCircle(sketch, "E9.0.1.1", {"center": v(70.61, -42.23) * mm, "radius": 2.38 * mm});
            skCircle(sketch, "E9.0.1.2", {"center": v(-83.31, -51.75) * mm, "radius": 2.38 * mm});
            skCircle(sketch, "E9.0.1.3", {"center": v(6.35, -32.7) * mm, "radius": 2.38 * mm});
            skCircle(sketch, "E9.0.1.4", {"center": v(-112.27, -61.28) * mm, "radius": 2.38 * mm});
            skCircle(sketch, "E9.0.1.5", {"center": v(93.22, -51.75) * mm, "radius": 2.38 * mm});
            skCircle(sketch, "E9.0.1.7", {"center": v(48, -51.75) * mm, "radius": 2.38 * mm});
            skCircle(sketch, "E9.0.1.8", {"center": v(-48, -51.75) * mm, "radius": 2.38 * mm});
            skCircle(sketch, "E9.0.1.9", {"center": v(-99.57, -51.75) * mm, "radius": 2.38 * mm});
            skCircle(sketch, "E9.0.1.10", {"center": v(28.96, -32.7) * mm, "radius": 2.38 * mm});
            skCircle(sketch, "E9.0.1.11", {"center": v(-22.6, -32.7) * mm, "radius": 2.38 * mm});
            skCircle(sketch, "E9.0.1.12", {"center": v(-93.22, -61.28) * mm, "radius": 2.38 * mm});
            skCircle(sketch, "E9.0.1.13", {"center": v(-93.22, -51.75) * mm, "radius": 2.38 * mm});
            skCircle(sketch, "E9.0.1.14", {"center": v(57.91, -51.75) * mm, "radius": 2.38 * mm});
            skCircle(sketch, "E9.0.1.15", {"center": v(-12.7, -61.28) * mm, "radius": 2.38 * mm});
            skCircle(sketch, "E9.0.1.16", {"center": v(6.35, -51.75) * mm, "radius": 2.38 * mm});
            skCircle(sketch, "E9.0.1.17", {"center": v(-57.91, -32.7) * mm, "radius": 2.38 * mm});
            skCircle(sketch, "E9.0.1.18", {"center": v(76.96, -32.7) * mm, "radius": 2.38 * mm});
            skCircle(sketch, "E9.0.1.19", {"center": v(41.66, -61.28) * mm, "radius": 2.38 * mm});
            skCircle(sketch, "E9.0.1.20", {"center": v(-93.22, -32.7) * mm, "radius": 2.38 * mm});
            skCircle(sketch, "E9.0.1.21", {"center": v(28.96, -61.28) * mm, "radius": 2.38 * mm});
            skCircle(sketch, "E9.0.1.22", {"center": v(41.66, -51.75) * mm, "radius": 2.38 * mm});
            skCircle(sketch, "E9.0.1.23", {"center": v(35.3, -42.23) * mm, "radius": 2.38 * mm});
            skCircle(sketch, "E9.0.1.24", {"center": v(-41.66, -42.23) * mm, "radius": 2.38 * mm});
            skCircle(sketch, "E9.0.1.25", {"center": v(-70.61, -61.28) * mm, "radius": 2.38 * mm});
            skCircle(sketch, "E9.0.1.26", {"center": v(12.7, -32.7) * mm, "radius": 2.38 * mm});
            skCircle(sketch, "E9.0.1.27", {"center": v(-64.26, -51.75) * mm, "radius": 2.38 * mm});
            skCircle(sketch, "E9.0.1.28", {"center": v(118.62, -42.23) * mm, "radius": 2.38 * mm});
            skCircle(sketch, "E9.0.1.29", {"center": v(112.27, -51.75) * mm, "radius": 2.38 * mm});
            skCircle(sketch, "E9.0.1.30", {"center": v(118.62, -61.28) * mm, "radius": 2.38 * mm});
            skCircle(sketch, "E9.0.1.31", {"center": v(93.22, -32.7) * mm, "radius": 2.38 * mm});
            skCircle(sketch, "E9.0.1.32", {"center": v(76.96, -51.75) * mm, "radius": 2.38 * mm});
            skCircle(sketch, "E9.0.1.33", {"center": v(28.96, -51.75) * mm, "radius": 2.38 * mm});
            skCircle(sketch, "E9.0.1.34", {"center": v(6.35, -61.28) * mm, "radius": 2.38 * mm});
            skCircle(sketch, "E9.0.1.35", {"center": v(-112.27, -32.7) * mm, "radius": 2.38 * mm});
            skCircle(sketch, "E9.0.1.36", {"center": v(-64.26, -61.28) * mm, "radius": 2.38 * mm});
            skCircle(sketch, "E9.0.1.37", {"center": v(-105.92, -51.75) * mm, "radius": 2.38 * mm});
            skCircle(sketch, "E9.0.1.38", {"center": v(-57.91, -51.75) * mm, "radius": 2.38 * mm});
            skCircle(sketch, "E9.0.1.39", {"center": v(48, -32.7) * mm, "radius": 2.38 * mm});
            skCircle(sketch, "E9.0.1.40", {"center": v(118.62, -51.75) * mm, "radius": 2.38 * mm});
            skCircle(sketch, "E9.0.1.41", {"center": v(-99.57, -61.28) * mm, "radius": 2.38 * mm});
            skCircle(sketch, "E9.0.1.42", {"center": v(6.35, -42.23) * mm, "radius": 2.38 * mm});
            skCircle(sketch, "E9.0.1.43", {"center": v(-28.96, -51.75) * mm, "radius": 2.38 * mm});
            skCircle(sketch, "E9.0.1.44", {"center": v(-105.92, -32.7) * mm, "radius": 2.38 * mm});
            skCircle(sketch, "E9.0.1.45", {"center": v(105.92, -51.75) * mm, "radius": 2.38 * mm});
            skCircle(sketch, "E9.0.1.46", {"center": v(-6.35, -32.7) * mm, "radius": 2.38 * mm});
            skCircle(sketch, "E9.0.1.47", {"center": v(99.57, -61.28) * mm, "radius": 2.38 * mm});
            skCircle(sketch, "E9.0.1.48", {"center": v(0, -51.75) * mm, "radius": 2.38 * mm});
            skCircle(sketch, "E9.0.1.49", {"center": v(-12.7, -51.75) * mm, "radius": 2.38 * mm});
            skCircle(sketch, "E9.0.1.50", {"center": v(-118.62, -61.28) * mm, "radius": 2.38 * mm});
            skCircle(sketch, "E9.0.1.51", {"center": v(-70.61, -51.75) * mm, "radius": 2.38 * mm});
            skCircle(sketch, "E9.0.1.52", {"center": v(-93.22, -42.23) * mm, "radius": 2.38 * mm});
            skCircle(sketch, "E9.0.1.53", {"center": v(64.26, -61.28) * mm, "radius": 2.38 * mm});
            skCircle(sketch, "E9.0.1.54", {"center": v(-22.6, -61.28) * mm, "radius": 2.38 * mm});
            skCircle(sketch, "E9.0.1.55", {"center": v(-70.61, -42.23) * mm, "radius": 2.38 * mm});
            skCircle(sketch, "E9.0.1.56", {"center": v(-41.66, -51.75) * mm, "radius": 2.38 * mm});
            skCircle(sketch, "E9.0.1.57", {"center": v(-22.6, -51.75) * mm, "radius": 2.38 * mm});
            skCircle(sketch, "E9.0.1.58", {"center": v(-105.92, -61.28) * mm, "radius": 2.38 * mm});
            skCircle(sketch, "E9.0.1.59", {"center": v(12.7, -51.75) * mm, "radius": 2.38 * mm});
            skCircle(sketch, "E9.0.1.60", {"center": v(93.22, -61.28) * mm, "radius": 2.38 * mm});
            skCircle(sketch, "E9.0.1.61", {"center": v(22.6, -32.7) * mm, "radius": 2.38 * mm});
            skCircle(sketch, "E9.0.1.62", {"center": v(-35.3, -61.28) * mm, "radius": 2.38 * mm});
            skCircle(sketch, "E9.0.1.63", {"center": v(-83.31, -42.23) * mm, "radius": 2.38 * mm});
            skCircle(sketch, "E9.0.1.64", {"center": v(-35.3, -32.7) * mm, "radius": 2.38 * mm});
            skCircle(sketch, "E9.0.1.65", {"center": v(12.7, -61.28) * mm, "radius": 2.38 * mm});
            skCircle(sketch, "E9.0.1.66", {"center": v(-70.61, -32.7) * mm, "radius": 2.38 * mm});
            skCircle(sketch, "E9.0.1.67", {"center": v(-83.31, -32.7) * mm, "radius": 2.38 * mm});
            skCircle(sketch, "E9.0.1.68", {"center": v(-35.3, -51.75) * mm, "radius": 2.38 * mm});
            skLineSegment(sketch, "E9.0.1.69", {"start": v(-12.7, -61.28) * mm, "end": v(22.6, -61.28) * mm, "construction": true});
            skCircle(sketch, "E9.0.1.70", {"center": v(-28.96, -32.7) * mm, "radius": 2.38 * mm});
            skCircle(sketch, "E9.0.1.71", {"center": v(35.3, -51.75) * mm, "radius": 2.38 * mm});
            skCircle(sketch, "E9.0.1.72", {"center": v(-76.96, -51.75) * mm, "radius": 2.38 * mm});
            skCircle(sketch, "E9.0.1.73", {"center": v(22.6, -42.23) * mm, "radius": 2.38 * mm});
            skCircle(sketch, "E9.0.1.74", {"center": v(105.92, -61.28) * mm, "radius": 2.38 * mm});
            skCircle(sketch, "E9.0.1.75", {"center": v(-22.6, -42.23) * mm, "radius": 2.38 * mm});
            skCircle(sketch, "E9.0.1.76", {"center": v(57.91, -32.7) * mm, "radius": 2.38 * mm});
            skCircle(sketch, "E9.0.1.77", {"center": v(83.31, -61.28) * mm, "radius": 2.38 * mm});
            skCircle(sketch, "E9.0.1.78", {"center": v(41.66, -32.7) * mm, "radius": 2.38 * mm});
            skCircle(sketch, "E9.0.1.79", {"center": v(-64.26, -32.7) * mm, "radius": 2.38 * mm});
            skCircle(sketch, "E9.0.1.80", {"center": v(70.61, -51.75) * mm, "radius": 2.38 * mm});
            skCircle(sketch, "E9.0.1.81", {"center": v(-112.27, -51.75) * mm, "radius": 2.38 * mm});
            skCircle(sketch, "E9.0.1.82", {"center": v(-12.7, -32.7) * mm, "radius": 2.38 * mm});
            skCircle(sketch, "E9.0.1.83", {"center": v(0, -32.7) * mm, "radius": 2.38 * mm});
            skCircle(sketch, "E9.0.1.84", {"center": v(-112.27, -42.23) * mm, "radius": 2.38 * mm});
            skCircle(sketch, "E9.0.1.85", {"center": v(-6.35, -42.23) * mm, "radius": 2.38 * mm});
            skCircle(sketch, "E9.0.1.86", {"center": v(-118.62, -51.75) * mm, "radius": 2.38 * mm});
            skCircle(sketch, "E9.0.1.87", {"center": v(-41.66, -61.28) * mm, "radius": 2.38 * mm});
            skCircle(sketch, "E9.0.1.88", {"center": v(0, -61.28) * mm, "radius": 2.38 * mm});
            skCircle(sketch, "E9.0.1.89", {"center": v(-28.96, -61.28) * mm, "radius": 2.38 * mm});
            skCircle(sketch, "E9.0.1.90", {"center": v(64.26, -51.75) * mm, "radius": 2.38 * mm});
            skCircle(sketch, "E9.0.1.91", {"center": v(-118.62, -32.7) * mm, "radius": 2.38 * mm});
            skCircle(sketch, "E9.0.1.92", {"center": v(-99.57, -32.7) * mm, "radius": 2.38 * mm});
            skCircle(sketch, "E9.0.1.93", {"center": v(99.57, -32.7) * mm, "radius": 2.38 * mm});
            skCircle(sketch, "E9.0.1.94", {"center": v(-48, -61.28) * mm, "radius": 2.38 * mm});
            skCircle(sketch, "E9.0.1.95", {"center": v(118.62, -32.7) * mm, "radius": 2.38 * mm});
            skCircle(sketch, "E9.0.1.96", {"center": v(83.31, -51.75) * mm, "radius": 2.38 * mm});
            skCircle(sketch, "E9.0.1.97", {"center": v(70.61, -61.28) * mm, "radius": 2.38 * mm});
            skCircle(sketch, "E9.0.1.98", {"center": v(105.92, -32.7) * mm, "radius": 2.38 * mm});
            skCircle(sketch, "E9.0.1.99", {"center": v(64.26, -32.7) * mm, "radius": 2.38 * mm});
            skCircle(sketch, "E9.0.1.100", {"center": v(22.6, -51.75) * mm, "radius": 2.38 * mm});
            skCircle(sketch, "E9.0.1.101", {"center": v(112.27, -32.7) * mm, "radius": 2.38 * mm});
            skCircle(sketch, "E9.0.1.102", {"center": v(-6.35, -51.75) * mm, "radius": 2.38 * mm});
            skCircle(sketch, "E9.0.1.103", {"center": v(99.57, -42.23) * mm, "radius": 2.38 * mm});
            skCircle(sketch, "E9.0.1.104", {"center": v(83.31, -42.23) * mm, "radius": 2.38 * mm});
            skCircle(sketch, "E9.0.1.105", {"center": v(70.61, -32.7) * mm, "radius": 2.38 * mm});
            skCircle(sketch, "E9.0.1.106", {"center": v(112.27, -61.28) * mm, "radius": 2.38 * mm});
            skCircle(sketch, "E9.0.1.107", {"center": v(22.6, -61.28) * mm, "radius": 2.38 * mm});
            skCircle(sketch, "E9.0.1.108", {"center": v(48, -61.28) * mm, "radius": 2.38 * mm});
            skCircle(sketch, "E9.0.1.109", {"center": v(83.31, -32.7) * mm, "radius": 2.38 * mm});
            skCircle(sketch, "E9.0.1.110", {"center": v(57.91, -61.28) * mm, "radius": 2.38 * mm});
            skCircle(sketch, "E9.0.1.111", {"center": v(35.3, -32.7) * mm, "radius": 2.38 * mm});
            skCircle(sketch, "E9.0.1.112", {"center": v(35.3, -61.28) * mm, "radius": 2.38 * mm});
            skCircle(sketch, "E9.0.1.113", {"center": v(76.96, -61.28) * mm, "radius": 2.38 * mm});
            skCircle(sketch, "E9.0.1.114", {"center": v(99.57, -51.75) * mm, "radius": 2.38 * mm});
            skCircle(sketch, "E9.0.1.115", {"center": v(-76.96, -32.7) * mm, "radius": 2.38 * mm});
            skCircle(sketch, "E9.0.1.116", {"center": v(-48, -32.7) * mm, "radius": 2.38 * mm});
            skCircle(sketch, "E9.0.1.117", {"center": v(-83.31, -61.28) * mm, "radius": 2.38 * mm});
            skCircle(sketch, "E9.0.1.118", {"center": v(-6.35, -61.28) * mm, "radius": 2.38 * mm});
            skCircle(sketch, "E9.0.1.119", {"center": v(-57.91, -61.28) * mm, "radius": 2.38 * mm});
            skCircle(sketch, "E9.0.1.120", {"center": v(-41.66, -32.7) * mm, "radius": 2.38 * mm});
            skCircle(sketch, "E9.0.1.121", {"center": v(-48, -42.23) * mm, "radius": 2.38 * mm});
            skCircle(sketch, "E9.0.1.122", {"center": v(76.96, -42.23) * mm, "radius": 2.38 * mm});
            skCircle(sketch, "E9.0.1.123", {"center": v(-12.7, -42.23) * mm, "radius": 2.38 * mm});
            skCircle(sketch, "E9.0.1.124", {"center": v(-118.62, -42.23) * mm, "radius": 2.38 * mm});
            skCircle(sketch, "E9.0.1.125", {"center": v(28.96, -42.23) * mm, "radius": 2.38 * mm});
            skCircle(sketch, "E9.0.1.126", {"center": v(-64.26, -42.23) * mm, "radius": 2.38 * mm});
            skCircle(sketch, "E9.0.1.127", {"center": v(12.7, -42.23) * mm, "radius": 2.38 * mm});
            skCircle(sketch, "E9.0.1.128", {"center": v(-76.96, -42.23) * mm, "radius": 2.38 * mm});
            skCircle(sketch, "E9.0.1.129", {"center": v(-57.91, -42.23) * mm, "radius": 2.38 * mm});
            skCircle(sketch, "E9.0.1.130", {"center": v(-99.57, -42.23) * mm, "radius": 2.38 * mm});
            skCircle(sketch, "E9.0.1.131", {"center": v(-105.92, -42.23) * mm, "radius": 2.38 * mm});
            skCircle(sketch, "E9.0.1.132", {"center": v(57.91, -42.23) * mm, "radius": 2.38 * mm});
            skCircle(sketch, "E9.0.1.133", {"center": v(-35.3, -42.23) * mm, "radius": 2.38 * mm});
            skCircle(sketch, "E9.0.1.134", {"center": v(0, -42.23) * mm, "radius": 2.38 * mm});
            skCircle(sketch, "E9.0.1.135", {"center": v(64.26, -42.23) * mm, "radius": 2.38 * mm});
            skCircle(sketch, "E9.0.1.136", {"center": v(112.27, -42.23) * mm, "radius": 2.38 * mm});
            skCircle(sketch, "E9.0.1.137", {"center": v(105.92, -42.23) * mm, "radius": 2.38 * mm});
            skCircle(sketch, "E9.0.1.138", {"center": v(93.22, -42.23) * mm, "radius": 2.38 * mm});
            skCircle(sketch, "E9.0.1.139", {"center": v(41.66, -42.23) * mm, "radius": 2.38 * mm});
            skCircle(sketch, "E9.0.1.140", {"center": v(-28.96, -42.23) * mm, "radius": 2.38 * mm});
            skCircle(sketch, "E9.0.1.141", {"center": v(48, -42.23) * mm, "radius": 2.38 * mm});
            skCircle(sketch, "E10.1.0.0", {"center": v(-147.57, 61.28) * mm, "radius": 2.38 * mm});
            skCircle(sketch, "E10.1.0.1", {"center": v(-128.52, 32.7) * mm, "radius": 2.38 * mm});
            skCircle(sketch, "E10.1.0.2", {"center": v(-128.52, 61.28) * mm, "radius": 2.38 * mm});
            skCircle(sketch, "E10.1.0.3", {"center": v(-134.87, 32.7) * mm, "radius": 2.38 * mm});
            skCircle(sketch, "E10.1.0.4", {"center": v(-141.22, 61.28) * mm, "radius": 2.38 * mm});
            skCircle(sketch, "E10.1.0.5", {"center": v(-134.87, 61.28) * mm, "radius": 2.38 * mm});
            skCircle(sketch, "E10.1.0.6", {"center": v(-153.92, 51.75) * mm, "radius": 2.38 * mm});
            skCircle(sketch, "E10.1.0.7", {"center": v(-134.87, 42.23) * mm, "radius": 2.38 * mm});
            skCircle(sketch, "E10.1.0.8", {"center": v(-147.57, 32.7) * mm, "radius": 2.38 * mm});
            skCircle(sketch, "E10.1.0.9", {"center": v(-134.87, 51.75) * mm, "radius": 2.38 * mm});
            skCircle(sketch, "E10.1.0.10", {"center": v(-153.92, 32.7) * mm, "radius": 2.38 * mm});
            skCircle(sketch, "E10.1.0.11", {"center": v(-128.52, 51.75) * mm, "radius": 2.38 * mm});
            skCircle(sketch, "E10.1.0.12", {"center": v(-141.22, 42.23) * mm, "radius": 2.38 * mm});
            skCircle(sketch, "E10.1.0.13", {"center": v(-141.22, 32.7) * mm, "radius": 2.38 * mm});
            skCircle(sketch, "E10.1.0.14", {"center": v(-128.52, 42.23) * mm, "radius": 2.38 * mm});
            skCircle(sketch, "E10.1.0.15", {"center": v(-147.57, 51.75) * mm, "radius": 2.38 * mm});
            skCircle(sketch, "E10.1.0.16", {"center": v(-141.22, 51.75) * mm, "radius": 2.38 * mm});
            skCircle(sketch, "E10.1.0.17", {"center": v(-153.92, 42.23) * mm, "radius": 2.38 * mm});
            skCircle(sketch, "E10.1.0.18", {"center": v(-153.92, 61.28) * mm, "radius": 2.38 * mm});
            skCircle(sketch, "E10.1.0.19", {"center": v(-147.57, 42.23) * mm, "radius": 2.38 * mm});
            skCircle(sketch, "E11.1.0.0", {"center": v(156.72, -51.75) * mm, "radius": 2.38 * mm});
            skCircle(sketch, "E11.1.0.1", {"center": v(156.72, -42.23) * mm, "radius": 2.38 * mm});
            skCircle(sketch, "E11.1.0.2", {"center": v(144.02, -61.28) * mm, "radius": 2.38 * mm});
            skCircle(sketch, "E11.1.0.3", {"center": v(156.72, -32.7) * mm, "radius": 2.38 * mm});
            skCircle(sketch, "E11.1.0.4", {"center": v(144.02, -42.23) * mm, "radius": 2.38 * mm});
            skCircle(sketch, "E11.1.0.5", {"center": v(144.02, -32.7) * mm, "radius": 2.38 * mm});
            skCircle(sketch, "E11.1.0.6", {"center": v(144.02, -51.75) * mm, "radius": 2.38 * mm});
            skCircle(sketch, "E11.1.0.7", {"center": v(150.37, -51.75) * mm, "radius": 2.38 * mm});
            skCircle(sketch, "E11.1.0.8", {"center": v(150.37, -32.7) * mm, "radius": 2.38 * mm});
            skCircle(sketch, "E11.1.0.9", {"center": v(150.37, -42.23) * mm, "radius": 2.38 * mm});
            skCircle(sketch, "E11.1.0.10", {"center": v(156.72, -61.28) * mm, "radius": 2.38 * mm});
            skCircle(sketch, "E11.1.0.11", {"center": v(150.37, -61.28) * mm, "radius": 2.38 * mm});
            skCircle(sketch, "E12.1.0.0", {"center": v(-131.7, -51.75) * mm, "radius": 2.38 * mm});
            skCircle(sketch, "E12.1.0.1", {"center": v(-131.7, -42.23) * mm, "radius": 2.38 * mm});
            skCircle(sketch, "E12.1.0.2", {"center": v(-131.7, -61.28) * mm, "radius": 2.38 * mm});
            skCircle(sketch, "E12.1.0.3", {"center": v(-131.7, -32.7) * mm, "radius": 2.38 * mm});
            skCircle(sketch, "E13.1.0", {"center": v(-151.68, -43.48) * mm, "radius": 2.38 * mm});
            skCircle(sketch, "E13.1.1", {"center": v(-144.94, -36.74) * mm, "radius": 2.38 * mm});
            skCircle(sketch, "E13.1.2", {"center": v(-158.42, -50.21) * mm, "radius": 2.38 * mm});
            skCircle(sketch, "E13.1.3", {"center": v(-138.2, -30) * mm, "radius": 2.38 * mm});
            skCircle(sketch, "E13.2.0", {"center": v(-159.96, -23.5) * mm, "radius": 2.38 * mm});
            skCircle(sketch, "E13.2.1", {"center": v(-150.43, -23.5) * mm, "radius": 2.38 * mm});
            skCircle(sketch, "E13.2.2", {"center": v(-169.48, -23.5) * mm, "radius": 2.38 * mm});
            skCircle(sketch, "E13.2.3", {"center": v(-140.9, -23.5) * mm, "radius": 2.38 * mm});
            skCircle(sketch, "E13.3.0", {"center": v(-151.68, -3.51) * mm, "radius": 2.38 * mm});
            skCircle(sketch, "E13.3.1", {"center": v(-144.94, -10.25) * mm, "radius": 2.38 * mm});
            skCircle(sketch, "E13.3.2", {"center": v(-158.42, 3.22) * mm, "radius": 2.38 * mm});
            skCircle(sketch, "E13.3.3", {"center": v(-138.2, -16.98) * mm, "radius": 2.38 * mm});
            skCircle(sketch, "E13.4.0", {"center": v(-131.7, 4.76) * mm, "radius": 2.38 * mm});
            skCircle(sketch, "E13.4.1", {"center": v(-131.7, -4.76) * mm, "radius": 2.38 * mm});
            skCircle(sketch, "E13.4.2", {"center": v(-131.7, 14.29) * mm, "radius": 2.38 * mm});
            skCircle(sketch, "E13.4.3", {"center": v(-131.7, -14.29) * mm, "radius": 2.38 * mm});
            skPoint(sketch, "E13.center", {"position": v(-131.7, -23.5) * mm});
            skCircle(sketch, "E14.1.0.0", {"center": v(128.52, 32.7) * mm, "radius": 2.38 * mm});
            skCircle(sketch, "E14.1.0.1", {"center": v(128.52, 42.23) * mm, "radius": 2.38 * mm});
            skCircle(sketch, "E14.1.0.2", {"center": v(128.52, 51.75) * mm, "radius": 2.38 * mm});
            skCircle(sketch, "E14.1.0.3", {"center": v(128.52, 61.28) * mm, "radius": 2.38 * mm});
            skCircle(sketch, "E15.1.0", {"center": v(148.5, 43.48) * mm, "radius": 2.38 * mm});
            skCircle(sketch, "E15.1.1", {"center": v(141.77, 36.74) * mm, "radius": 2.38 * mm});
            skCircle(sketch, "E15.1.2", {"center": v(155.24, 50.21) * mm, "radius": 2.38 * mm});
            skCircle(sketch, "E15.1.3", {"center": v(135.03, 30) * mm, "radius": 2.38 * mm});
            skCircle(sketch, "E15.2.0", {"center": v(156.78, 23.5) * mm, "radius": 2.38 * mm});
            skCircle(sketch, "E15.2.1", {"center": v(147.26, 23.5) * mm, "radius": 2.38 * mm});
            skCircle(sketch, "E15.2.2", {"center": v(166.3, 23.5) * mm, "radius": 2.38 * mm});
            skCircle(sketch, "E15.2.3", {"center": v(137.73, 23.5) * mm, "radius": 2.38 * mm});
            skCircle(sketch, "E15.3.0", {"center": v(148.5, 3.51) * mm, "radius": 2.38 * mm});
            skCircle(sketch, "E15.3.1", {"center": v(141.77, 10.25) * mm, "radius": 2.38 * mm});
            skCircle(sketch, "E15.3.2", {"center": v(155.24, -3.22) * mm, "radius": 2.38 * mm});
            skCircle(sketch, "E15.3.3", {"center": v(135.03, 16.98) * mm, "radius": 2.38 * mm});
            skCircle(sketch, "E15.4.0", {"center": v(128.52, -4.76) * mm, "radius": 2.38 * mm});
            skCircle(sketch, "E15.4.1", {"center": v(128.52, 4.76) * mm, "radius": 2.38 * mm});
            skCircle(sketch, "E15.4.2", {"center": v(128.52, -14.29) * mm, "radius": 2.38 * mm});
            skCircle(sketch, "E15.4.3", {"center": v(128.52, 14.29) * mm, "radius": 2.38 * mm});
            skPoint(sketch, "E15.center", {"position": v(128.52, 23.5) * mm});
            skCircle(sketch, "E16", {"center": v(-168.21, 47) * mm, "radius": 2.38 * mm});
            skSolve(sketch);
        }
        {
            var Q0;
            Q0=makeQuery(id+"F1.opExtrude","CAP_FACE",FACE,{"disambiguationData":[OSD([sQuery(id+"F0.wireOp",EDGE,"E0.bottom"),sQuery(id+"F0.wireOp",EDGE,"E0.top"),sQuery(id+"F0.wireOp",EDGE,"E0.left"),sQuery(id+"F0.wireOp",EDGE,"E0.right")])],"isStart":false});
            var sketch = newSketch(context, id + "F3", { "sketchPlane" : qUnion([Q0])});
            skPoint(sketch, "E17.middle", {"position": v(75.34, 0) * mm});
            skPoint(sketch, "E18.middle", {"position": v(-86, 0) * mm});
            skCircle(sketch, "E19", {"center": v(-171.45, 57.15) * mm, "radius": 4 * mm});
            skCircle(sketch, "E20", {"center": v(171.45, 57.15) * mm, "radius": 4 * mm});
            skSolve(sketch);
        }
        {
            var Q0;
            Q0 = qSketchRegion(id + "F2", true);
            extrude(context, id + "F4", {"entities" : qUnion([Q0]), "operationType" : NewBodyOperationType.REMOVE, "oppositeDirection" : true, "depth" : 9.52 * mm, "offsetDistance" : 25 * mm});
        }
        {
            var Q0;
            Q0=makeQuery(id+"F3.imprint","IMPRINT",FACE,{"disambiguationData":[TD([[makeQuery(id+"F3.imprint","IMPRINT",EDGE,{"derivedFrom":sQuery(id+"F3.wireOp",EDGE,"E19")}),1.0]])]});
            var Q1;
            Q1=makeQuery(id+"F3.imprint","IMPRINT",FACE,{"disambiguationData":[TD([[makeQuery(id+"F3.imprint","IMPRINT",EDGE,{"derivedFrom":sQuery(id+"F3.wireOp",EDGE,"E20")}),1.0]])]});
            extrude(context, id + "F5", {"entities" : qUnion([Q0, Q1]), "operationType" : NewBodyOperationType.REMOVE, "oppositeDirection" : true, "depth" : 5 * mm, "offsetDistance" : 25 * mm});
        }
        {
            var Q0;
            Q0=makeQuery(id+"F1.opExtrude","CAP_FACE",FACE,{"disambiguationData":[OSD([sQuery(id+"F0.wireOp",EDGE,"E0.bottom"),sQuery(id+"F0.wireOp",EDGE,"E0.top"),sQuery(id+"F0.wireOp",EDGE,"E0.left"),sQuery(id+"F0.wireOp",EDGE,"E0.right")])],"isStart":true});
            var sketch = newSketch(context, id + "F6", { "sketchPlane" : qUnion([Q0])});
            skLineSegment(sketch, "E21.bottom", {"start": v(138.94, -27.62) * mm, "end": v(161.8, -27.62) * mm});
            skLineSegment(sketch, "E21.top", {"start": v(138.94, -66.36) * mm, "end": v(161.8, -66.36) * mm});
            skLineSegment(sketch, "E21.right", {"start": v(161.8, -27.62) * mm, "end": v(161.8, -66.36) * mm});
            skLineSegment(sketch, "E22.bottom", {"start": v(-160.27, 39.05) * mm, "end": v(-176.15, 39.05) * mm});
            skLineSegment(sketch, "E22.top", {"start": v(-160.27, 54.93) * mm, "end": v(-176.15, 54.93) * mm});
            skLineSegment(sketch, "E22.right", {"start": v(-176.15, 39.05) * mm, "end": v(-176.15, 54.93) * mm});
            skPoint(sketch, "E22.middle", {"position": v(-168.21, 47) * mm});
            skArc(sketch, "E23", {"start": v(128.14, 66.36) * mm, "mid": v(171, 23.5) * mm, "end": v(128.14, -19.37) * mm});
            skArc(sketch, "E24", {"start": v(128.14, 27.62) * mm, "mid": v(132.27, 23.5) * mm, "end": v(128.14, 19.37) * mm});
            skArc(sketch, "E25", {"start": v(-131.32, 19.37) * mm, "mid": v(-174.18, -23.5) * mm, "end": v(-131.32, -66.36) * mm});
            skArc(sketch, "E26", {"start": v(-131.32, -19.37) * mm, "mid": v(-135.45, -23.5) * mm, "end": v(-131.32, -27.62) * mm});
            skLineSegment(sketch, "E27", {"start": v(124.97, -27.62) * mm, "end": v(124.97, -66.36) * mm});
            skLineSegment(sketch, "E28", {"start": v(138.94, -27.62) * mm, "end": v(138.94, -66.36) * mm});
            skLineSegment(sketch, "E29", {"start": v(-160.27, 66.36) * mm, "end": v(-160.27, 54.93) * mm});
            skLineSegment(sketch, "E30", {"start": v(-160.27, 39.05) * mm, "end": v(-160.27, 27.62) * mm});
            skLineSegment(sketch, "E31", {"start": v(-160.27, 66.36) * mm, "end": v(128.14, 66.36) * mm});
            skLineSegment(sketch, "E32", {"start": v(128.14, 27.62) * mm, "end": v(-160.27, 27.62) * mm});
            skLineSegment(sketch, "E33", {"start": v(-131.32, 19.37) * mm, "end": v(128.14, 19.37) * mm});
            skLineSegment(sketch, "E34", {"start": v(128.14, -19.37) * mm, "end": v(-131.32, -19.37) * mm});
            skLineSegment(sketch, "E35", {"start": v(-131.32, -27.62) * mm, "end": v(124.97, -27.62) * mm});
            skLineSegment(sketch, "E36", {"start": v(124.97, -66.36) * mm, "end": v(-131.32, -66.36) * mm});
            skSolve(sketch);
        }
        {
            var Q0;
            Q0=makeQuery(id+"F6.imprint","IMPRINT",FACE,{"disambiguationData":[TD([[makeQuery(id+"F6.imprint","IMPRINT",EDGE,{"derivedFrom":sQuery(id+"F6.wireOp",EDGE,"E21.bottom")}),-1.0]])]});
            var Q1;
            Q1=makeQuery(id+"F6.imprint","IMPRINT",FACE,{"disambiguationData":[TD([[makeQuery(id+"F6.imprint","IMPRINT",EDGE,{"derivedFrom":sQuery(id+"F6.wireOp",EDGE,"E22.bottom")}),-1.0]])]});
            extrude(context, id + "F7", {"entities" : qUnion([Q0, Q1]), "operationType" : NewBodyOperationType.REMOVE, "oppositeDirection" : true, "depth" : 3.17 * mm, "offsetDistance" : 25.4 * mm});
        }
        {
            var Q0;
            Q0=makeQuery(id+"F7.boolean.opBoolean","COPY",EDGE,{"derivedFrom":makeQuery(id+"F7.opExtrude","SWEPT_EDGE",EDGE,{"disambiguationData":[OSD([sQuery(id+"F6.wireOp",EDGE,"E21.bottom"),sQuery(id+"F6.wireOp",EDGE,"E21.right")])]})});
            var Q1;
            Q1=makeQuery(id+"F7.boolean.opBoolean","COPY",EDGE,{"derivedFrom":makeQuery(id+"F7.opExtrude","SWEPT_EDGE",EDGE,{"disambiguationData":[OSD([sQuery(id+"F6.wireOp",EDGE,"4y3J7fxc-65ja-srwX-CFLx-9xzcbfl7g7d0"),sQuery(id+"F6.wireOp",EDGE,"E27")])]})});
            var Q2;
            Q2=makeQuery(id+"F7.boolean.opBoolean","COPY",EDGE,{"derivedFrom":makeQuery(id+"F7.opExtrude","SWEPT_EDGE",EDGE,{"disambiguationData":[OSD([sQuery(id+"F6.wireOp",EDGE,"E21.bottom"),sQuery(id+"F6.wireOp",EDGE,"E28")])]})});
            var Q3;
            Q3=makeQuery(id+"F7.boolean.opBoolean","COPY",EDGE,{"derivedFrom":makeQuery(id+"F7.opExtrude","SWEPT_EDGE",EDGE,{"disambiguationData":[OSD([sQuery(id+"F6.wireOp",EDGE,"E21.top"),sQuery(id+"F6.wireOp",EDGE,"E28")])]})});
            var Q4;
            Q4=makeQuery(id+"F7.boolean.opBoolean","COPY",EDGE,{"derivedFrom":makeQuery(id+"F7.opExtrude","SWEPT_EDGE",EDGE,{"disambiguationData":[OSD([sQuery(id+"F6.wireOp",EDGE,"4pf7jCQY-lT75-MMVF-PmEa-bUmLlGaYWIa0"),sQuery(id+"F6.wireOp",EDGE,"E27")])]})});
            var Q5;
            Q5=makeQuery(id+"F7.boolean.opBoolean","COPY",EDGE,{"derivedFrom":makeQuery(id+"F7.opExtrude","SWEPT_EDGE",EDGE,{"disambiguationData":[OSD([sQuery(id+"F6.wireOp",EDGE,"E21.top"),sQuery(id+"F6.wireOp",EDGE,"E21.right")])]})});
            var Q6;
            Q6=makeQuery(id+"F7.boolean.opBoolean","COPY",EDGE,{"derivedFrom":makeQuery(id+"F7.opExtrude","SWEPT_EDGE",EDGE,{"disambiguationData":[OSD([sQuery(id+"F6.wireOp",EDGE,"E22.bottom"),sQuery(id+"F6.wireOp",EDGE,"E30")])]})});
            var Q7;
            Q7=makeQuery(id+"F7.boolean.opBoolean","COPY",EDGE,{"derivedFrom":makeQuery(id+"F7.opExtrude","SWEPT_EDGE",EDGE,{"disambiguationData":[OSD([sQuery(id+"F6.wireOp",EDGE,"E22.top"),sQuery(id+"F6.wireOp",EDGE,"E22.right")])]})});
            var Q8;
            Q8=makeQuery(id+"F7.boolean.opBoolean","COPY",EDGE,{"derivedFrom":makeQuery(id+"F7.opExtrude","SWEPT_EDGE",EDGE,{"disambiguationData":[OSD([sQuery(id+"F6.wireOp",EDGE,"E22.top"),sQuery(id+"F6.wireOp",EDGE,"E29")])]})});
            var Q9;
            Q9=makeQuery(id+"F7.boolean.opBoolean","COPY",EDGE,{"derivedFrom":makeQuery(id+"F7.opExtrude","SWEPT_EDGE",EDGE,{"disambiguationData":[OSD([sQuery(id+"F6.wireOp",EDGE,"0zDFIoZL-3A3E-ba8z-vHWR-BYIfueAvfeXo.bottom"),sQuery(id+"F6.wireOp",EDGE,"E29")])]})});
            var Q10;
            Q10=makeQuery(id+"F7.boolean.opBoolean","COPY",EDGE,{"derivedFrom":makeQuery(id+"F7.opExtrude","SWEPT_EDGE",EDGE,{"disambiguationData":[OSD([sQuery(id+"F6.wireOp",EDGE,"IVUHSJ4b-zM8l-sWFa-EgzE-pU9jkxoAxTL1"),sQuery(id+"F6.wireOp",EDGE,"E30")])]})});
            var Q11;
            Q11=makeQuery(id+"F7.boolean.opBoolean","COPY",EDGE,{"derivedFrom":makeQuery(id+"F7.opExtrude","SWEPT_EDGE",EDGE,{"disambiguationData":[OSD([sQuery(id+"F6.wireOp",EDGE,"E22.bottom"),sQuery(id+"F6.wireOp",EDGE,"E22.right")])]})});
            fillet(context, id + "F8", {"entities" : qUnion([Q0, Q1, Q2, Q3, Q4, Q5, Q6, Q7, Q8, Q9, Q10, Q11]), "radius" : 3.17 * mm, "tangentPropagation" : true, "allowEdgeOverflow" : false});
        }
        {
            var Q0;
            Q0=makeQuery(id+"F1.opExtrude","CAP_FACE",FACE,{"disambiguationData":[OSD([sQuery(id+"F0.wireOp",EDGE,"E0.bottom"),sQuery(id+"F0.wireOp",EDGE,"E0.top"),sQuery(id+"F0.wireOp",EDGE,"E0.left"),sQuery(id+"F0.wireOp",EDGE,"E0.right")])],"isStart":false});
            var sketch = newSketch(context, id + "F9", { "sketchPlane" : qUnion([Q0])});
            skCircle(sketch, "E37", {"center": v(170.5, -66.2) * mm, "radius": 5 * mm});
            skCircle(sketch, "E38", {"center": v(-170.5, -66.2) * mm, "radius": 5 * mm});
            skSolve(sketch);
        }
        {
            var Q0;
            Q0=makeQuery(id+"F9.imprint","IMPRINT",FACE,{"disambiguationData":[TD([[makeQuery(id+"F9.imprint","IMPRINT",EDGE,{"derivedFrom":sQuery(id+"F9.wireOp",EDGE,"E38")}),1.0]])]});
            var Q1;
            Q1=makeQuery(id+"F9.imprint","IMPRINT",FACE,{"disambiguationData":[TD([[makeQuery(id+"F9.imprint","IMPRINT",EDGE,{"derivedFrom":sQuery(id+"F9.wireOp",EDGE,"E37")}),1.0]])]});
            extrude(context, id + "F10", {"entities" : qUnion([Q0, Q1]), "operationType" : NewBodyOperationType.REMOVE, "oppositeDirection" : true, "depth" : 12 * mm, "offsetDistance" : 25 * mm});
        }
        {
            var Q0;
            Q0=makeQuery(id+"F1.opExtrude","SWEPT_FACE",FACE,{"disambiguationData":[OSD([sQuery(id+"F0.wireOp",EDGE,"E0.bottom")])]});
            var sketch = newSketch(context, id + "F11", { "sketchPlane" : qUnion([Q0])});
            skLineSegment(sketch, "E39.top", {"start": v(38.08, -15.88) * mm, "end": v(0, -15.88) * mm});
            skLineSegment(sketch, "E39.left", {"start": v(38.08, -6.35) * mm, "end": v(38.08, -15.88) * mm});
            skLineSegment(sketch, "E40.bottom", {"start": v(38.08, -6.35) * mm, "end": v(-38.08, -6.35) * mm});
            skLineSegment(sketch, "E40.top", {"start": v(38.08, -25.4) * mm, "end": v(-38.08, -25.4) * mm});
            skLineSegment(sketch, "E40.left", {"start": v(38.08, -6.35) * mm, "end": v(38.08, -25.4) * mm});
            skLineSegment(sketch, "E40.right", {"start": v(-38.08, -6.35) * mm, "end": v(-38.08, -25.4) * mm});
            skPoint(sketch, "E40.middle", {"position": v(0, -15.88) * mm});
            skSolve(sketch);
        }
        {
            var Q0;
            {var subQ1=sQuery(id+"F11.wireOp",EDGE,"E39.top");Q0=makeQuery(id+"F11.imprint","IMPRINT",FACE,{"disambiguationData":[TD([[makeQuery(id+"F11.imprint","IMPRINT",EDGE,{"derivedFrom":subQ1}),-1.0]])]});}
            extrude(context, id + "F12", {"entities" : qUnion([Q0]), "operationType" : NewBodyOperationType.REMOVE, "oppositeDirection" : true, "depth" : 6.35 * mm, "offsetDistance" : 25.4 * mm});
        }
        {
            var Q0;
            Q0=makeQuery(id+"F12.boolean.opBoolean","COPY",EDGE,{"derivedFrom":makeQuery(id+"F12.opExtrude","CAP_EDGE",EDGE,{"disambiguationData":[OSD([sQuery(id+"F11.wireOp",EDGE,"E40.bottom")])],"isStart":false})});
            var Q1;
            Q1=makeQuery(id+"F12.boolean.opBoolean","COPY",EDGE,{"derivedFrom":makeQuery(id+"F12.opExtrude","CAP_EDGE",EDGE,{"disambiguationData":[OSD([sQuery(id+"F11.wireOp",EDGE,"E39.left")])],"isStart":false})});
            var Q2;
            Q2=makeQuery(id+"F12.boolean.opBoolean","COPY",EDGE,{"derivedFrom":makeQuery(id+"F12.opExtrude","SWEPT_EDGE",EDGE,{"disambiguationData":[OSD([sQuery(id+"F11.wireOp",EDGE,"E40.bottom"),sQuery(id+"F11.wireOp",EDGE,"E40.right")])]})});
            var Q3;
            Q3=makeQuery(id+"F12.boolean.opBoolean","COPY",EDGE,{"derivedFrom":makeQuery(id+"F12.opExtrude","SWEPT_EDGE",EDGE,{"disambiguationData":[OSD([sQuery(id+"F11.wireOp",EDGE,"E39.left"),sQuery(id+"F11.wireOp",EDGE,"E40.bottom")])]})});
            var Q4;
            Q4=makeQuery(id+"F12.boolean.opBoolean","COPY",EDGE,{"derivedFrom":makeQuery(id+"F12.opExtrude","CAP_EDGE",EDGE,{"disambiguationData":[OSD([sQuery(id+"F11.wireOp",EDGE,"E40.right")])],"isStart":false})});
            fillet(context, id + "F13", {"entities" : qUnion([Q0, Q1, Q2, Q3, Q4]), "radius" : 6.35 * mm, "tangentPropagation" : true, "allowEdgeOverflow" : false});
        }
        {
            var Q0;
            Q0=makeQuery(id+"F1.opExtrude","CAP_FACE",FACE,{"disambiguationData":[OSD([sQuery(id+"F0.wireOp",EDGE,"E0.bottom"),sQuery(id+"F0.wireOp",EDGE,"E0.top"),sQuery(id+"F0.wireOp",EDGE,"E0.left"),sQuery(id+"F0.wireOp",EDGE,"E0.right")])],"isStart":false});
            var sketch = newSketch(context, id + "F14", { "sketchPlane" : qUnion([Q0])});
            skLineSegment(sketch, "E41", {"start": v(190.5, 16.7) * mm, "end": v(142.88, 16.7) * mm});
            skLineSegment(sketch, "E42", {"start": v(125.58, 76.2) * mm, "end": v(125.58, 34.93) * mm});
            skLineSegment(sketch, "E43.bottom", {"start": v(142.88, 34.93) * mm, "end": v(47.63, 34.93) * mm});
            skLineSegment(sketch, "E43.top", {"start": v(142.88, -34.92) * mm, "end": v(47.63, -34.92) * mm});
            skLineSegment(sketch, "E43.left", {"start": v(142.88, 34.93) * mm, "end": v(142.88, -34.92) * mm});
            skLineSegment(sketch, "E43.right", {"start": v(47.63, 34.93) * mm, "end": v(47.63, -34.92) * mm});
            skSolve(sketch);
        }
        {
            var Q0;
            {var subQ4=sQuery(id+"F14.wireOp",EDGE,"E43.top");Q0=makeQuery(id+"F14.imprint","IMPRINT",FACE,{"disambiguationData":[TD([[makeQuery(id+"F14.imprint","IMPRINT",EDGE,{"derivedFrom":subQ4}),-1.0]])]});}
            extrude(context, id + "F15", {"entities" : qUnion([Q0]), "operationType" : NewBodyOperationType.REMOVE, "oppositeDirection" : true, "depth" : 4.76 * mm, "offsetDistance" : 25.4 * mm});
        }
        {
            var Q0;
            Q0=makeQuery(id+"F15.boolean.opBoolean","COPY",EDGE,{"derivedFrom":makeQuery(id+"F15.opExtrude","SWEPT_EDGE",EDGE,{"disambiguationData":[OSD([sQuery(id+"F14.wireOp",EDGE,"E43.top"),sQuery(id+"F14.wireOp",EDGE,"E43.left")])]})});
            var Q1;
            Q1=makeQuery(id+"F15.boolean.opBoolean","COPY",EDGE,{"derivedFrom":makeQuery(id+"F15.opExtrude","SWEPT_EDGE",EDGE,{"disambiguationData":[OSD([sQuery(id+"F14.wireOp",EDGE,"E43.top"),sQuery(id+"F14.wireOp",EDGE,"E43.right")])]})});
            var Q2;
            Q2=makeQuery(id+"F15.boolean.opBoolean","COPY",EDGE,{"derivedFrom":makeQuery(id+"F15.opExtrude","SWEPT_EDGE",EDGE,{"disambiguationData":[OSD([sQuery(id+"F14.wireOp",EDGE,"E43.bottom"),sQuery(id+"F14.wireOp",EDGE,"E43.right")])]})});
            var Q3;
            Q3=makeQuery(id+"F15.boolean.opBoolean","COPY",EDGE,{"derivedFrom":makeQuery(id+"F15.opExtrude","SWEPT_EDGE",EDGE,{"disambiguationData":[OSD([sQuery(id+"F14.wireOp",EDGE,"E43.bottom"),sQuery(id+"F14.wireOp",EDGE,"E43.left")])]})});
            fillet(context, id + "F16", {"entities" : qUnion([Q0, Q1, Q2, Q3]), "radius" : 3.17 * mm, "tangentPropagation" : true, "allowEdgeOverflow" : false});
        }
        {
            var Q0;
            Q0=makeQuery(id+"F1.opExtrude","SWEPT_EDGE",EDGE,{"disambiguationData":[OSD([sQuery(id+"F0.wireOp",EDGE,"E0.bottom"),sQuery(id+"F0.wireOp",EDGE,"E0.right")])]});
            var Q1;
            Q1=makeQuery(id+"F1.opExtrude","SWEPT_EDGE",EDGE,{"disambiguationData":[OSD([sQuery(id+"F0.wireOp",EDGE,"E0.bottom"),sQuery(id+"F0.wireOp",EDGE,"E0.left")])]});
            var Q2;
            Q2=makeQuery(id+"F1.opExtrude","SWEPT_EDGE",EDGE,{"disambiguationData":[OSD([sQuery(id+"F0.wireOp",EDGE,"E0.top"),sQuery(id+"F0.wireOp",EDGE,"E0.left")])]});
            var Q3;
            Q3=makeQuery(id+"F1.opExtrude","SWEPT_EDGE",EDGE,{"disambiguationData":[OSD([sQuery(id+"F0.wireOp",EDGE,"E0.top"),sQuery(id+"F0.wireOp",EDGE,"E0.right")])]});
            fillet(context, id + "F17", {"entities" : qUnion([Q0, Q1, Q2, Q3]), "radius" : 3.17 * mm, "tangentPropagation" : true, "allowEdgeOverflow" : false});
        }
    });
